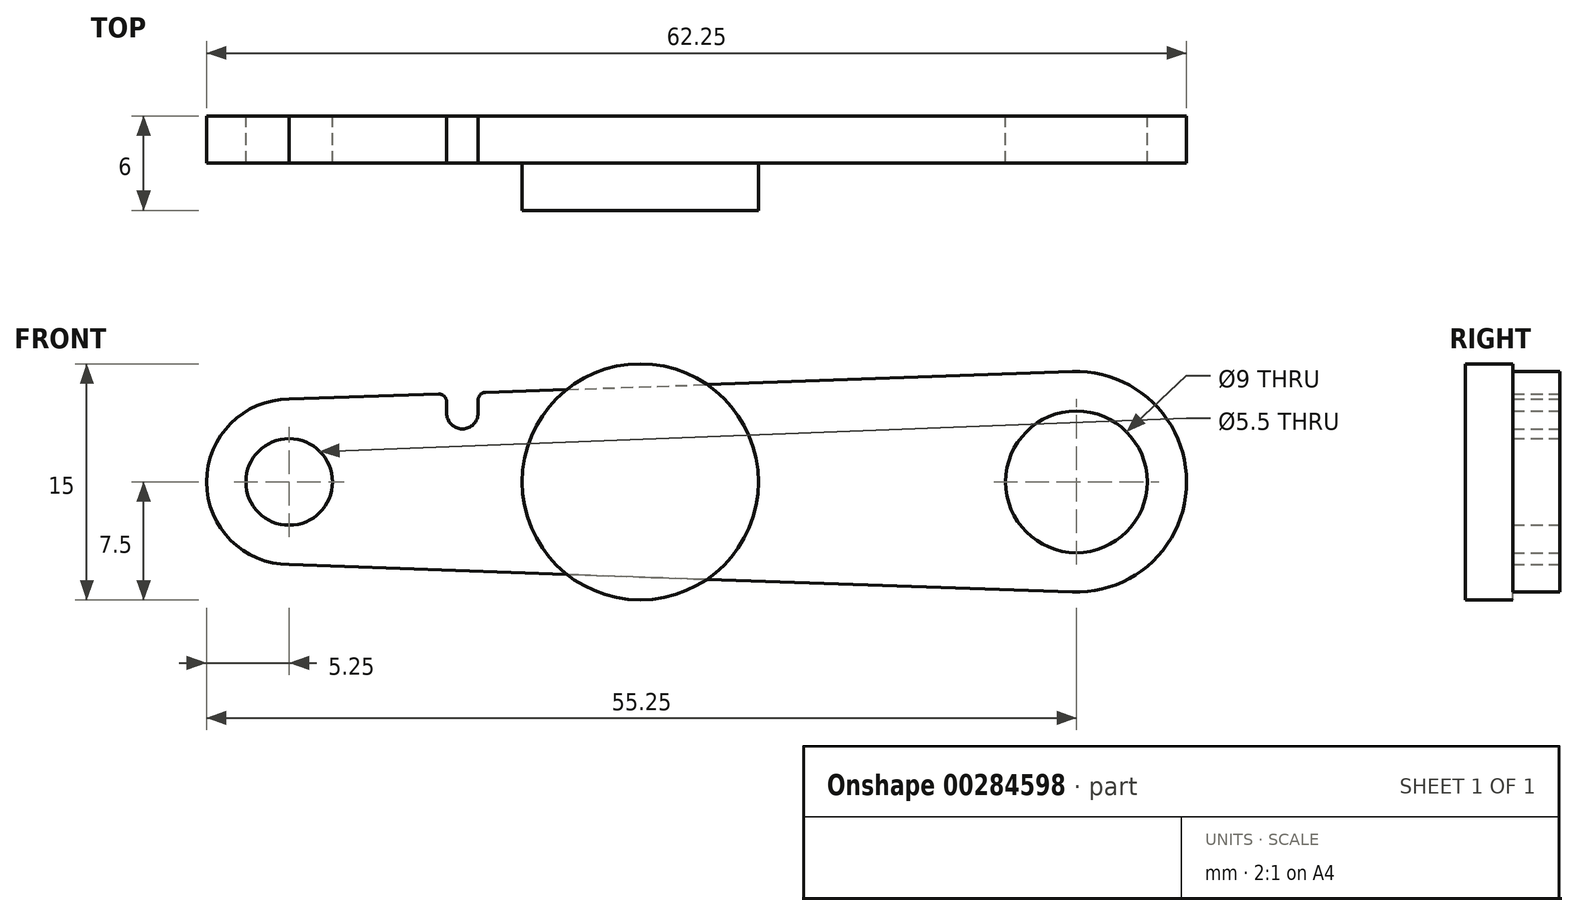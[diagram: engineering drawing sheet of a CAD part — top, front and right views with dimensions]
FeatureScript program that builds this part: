
annotation { "Feature Type Name" : "Feature", "Feature Type Description" : "" }
export const myFeature = defineFeature(function(context is Context, id is Id, definition is map)
    precondition{}
    {
        {
            var Q0;
            Q0=qCreatedBy(makeId("Front.planeOp"),FACE);
            var sketch = newSketch(context, id + "F0", { "sketchPlane" : qUnion([Q0])});
            skCircle(sketch, "E0", {"center": v(0, 0) * mm, "radius": 4.5 * mm});
            skArc(sketch, "E1", {"start": v(-0.25, -7) * mm, "mid": v(7, 0) * mm, "end": v(-0.25, 7) * mm});
            skCircle(sketch, "E2", {"center": v(-50, 0) * mm, "radius": 2.75 * mm});
            skArc(sketch, "E3", {"start": v(-50, 5.25) * mm, "mid": v(-55.25, 0) * mm, "end": v(-50, -5.25) * mm});
            skLineSegment(sketch, "E4", {"start": v(-50, 0) * mm, "end": v(0, 0) * mm, "construction": true});
            skLineSegment(sketch, "E5", {"start": v(-50, 5.25) * mm, "end": v(-40.52, 5.58) * mm});
            skLineSegment(sketch, "E6", {"start": v(-50, -5.25) * mm, "end": v(0, -7) * mm});
            skLineSegment(sketch, "E7", {"start": v(-50, 5.25) * mm, "end": v(-50, -5.25) * mm, "construction": true});
            skLineSegment(sketch, "E8", {"start": v(-40, 5.08) * mm, "end": v(-40, 4.37) * mm});
            skLineSegment(sketch, "E9", {"start": v(-38, 4.37) * mm, "end": v(-38, 5.19) * mm});
            skLineSegment(sketch, "E10", {"start": v(-38.94, 3.37) * mm, "end": v(-38.94, 3.37) * mm});
            skPoint(sketch, "E11.visualSharp", {"position": v(-40, 3.6) * mm});
            skArc(sketch, "E11.filletArc", {"start": v(-40, 4.37) * mm, "mid": v(-39.69, 3.64) * mm, "end": v(-38.94, 3.37) * mm});
            skPoint(sketch, "E12.visualSharp", {"position": v(-38, 3.67) * mm});
            skArc(sketch, "E12.filletArc", {"start": v(-38.94, 3.37) * mm, "mid": v(-38.27, 3.68) * mm, "end": v(-38, 4.37) * mm});
            skLineSegment(sketch, "E13.trimOffspring", {"start": v(-37.52, 5.69) * mm, "end": v(0, 7) * mm});
            skPoint(sketch, "E14.visualSharp", {"position": v(-40, 5.6) * mm});
            skArc(sketch, "E14.filletArc", {"start": v(-40, 5.08) * mm, "mid": v(-40.15, 5.44) * mm, "end": v(-40.52, 5.58) * mm});
            skPoint(sketch, "E15.visualSharp", {"position": v(-38, 5.67) * mm});
            skArc(sketch, "E15.filletArc", {"start": v(-37.52, 5.69) * mm, "mid": v(-37.86, 5.54) * mm, "end": v(-38, 5.19) * mm});
            skSolve(sketch);
        }
        {
            var Q0;
            {var subQ0=sQuery(id+"F0.wireOp",EDGE,"qNFY2Rbi-jpM3-P3Cz-0xK0-iVjeH50YWgXQ");Q0=makeQuery(id+"F0.imprint","IMPRINT",FACE,{"disambiguationData":[TD([[makeQuery(id+"F0.imprint","IMPRINT",EDGE,{"derivedFrom":subQ0}),-1.0]])]});}
            var Q1;
            Q1=makeQuery(id+"F0.imprint","IMPRINT",FACE,{"disambiguationData":[TD([[makeQuery(id+"F0.imprint","IMPRINT",EDGE,{"derivedFrom":sQuery(id+"F0.wireOp",EDGE,"E0")}),-1.0]])]});
            var Q2;
            Q2=makeQuery(id+"F0.imprint","IMPRINT",FACE,{"disambiguationData":[TD([[makeQuery(id+"F0.imprint","IMPRINT",EDGE,{"derivedFrom":sQuery(id+"F0.wireOp",EDGE,"E2")}),-1.0]])]});
            extrude(context, id + "F1", {"entities" : qUnion([Q0, Q1, Q2]), "depth" : 3 * mm});
        }
        {
            var Q0;
            Q0=qCreatedBy(makeId("Front.planeOp"),FACE);
            var sketch = newSketch(context, id + "F2", { "sketchPlane" : qUnion([Q0])});
            skCircle(sketch, "E16", {"center": v(-27.7, 0) * mm, "radius": 7.5 * mm});
            skSolve(sketch);
        }
        {
            var Q0;
            Q0=makeQuery(id+"F2.imprint","IMPRINT",FACE,{"disambiguationData":[TD([[makeQuery(id+"F2.imprint","IMPRINT",EDGE,{"derivedFrom":sQuery(id+"F2.wireOp",EDGE,"E16")}),1.0]])]});
            extrude(context, id + "F3", {"entities" : qUnion([Q0]), "depth" : 3 * mm});
        }
        {
            var Q0;
            Q0=makeQuery(id+"F3.opExtrude","SWEPT_BODY",BODY,{"disambiguationData":[OSD([sQuery(id+"F2.wireOp",EDGE,"E16")])]});
            transform(context, id + "F4", {"entities" : qUnion([Q0]), "transformType" : TransformType.TRANSLATION_3D, "dx" : 0 * mm, "dy" : -3 * mm, "dz" : 0 * mm, "makeCopy" : false});
        }
    });
